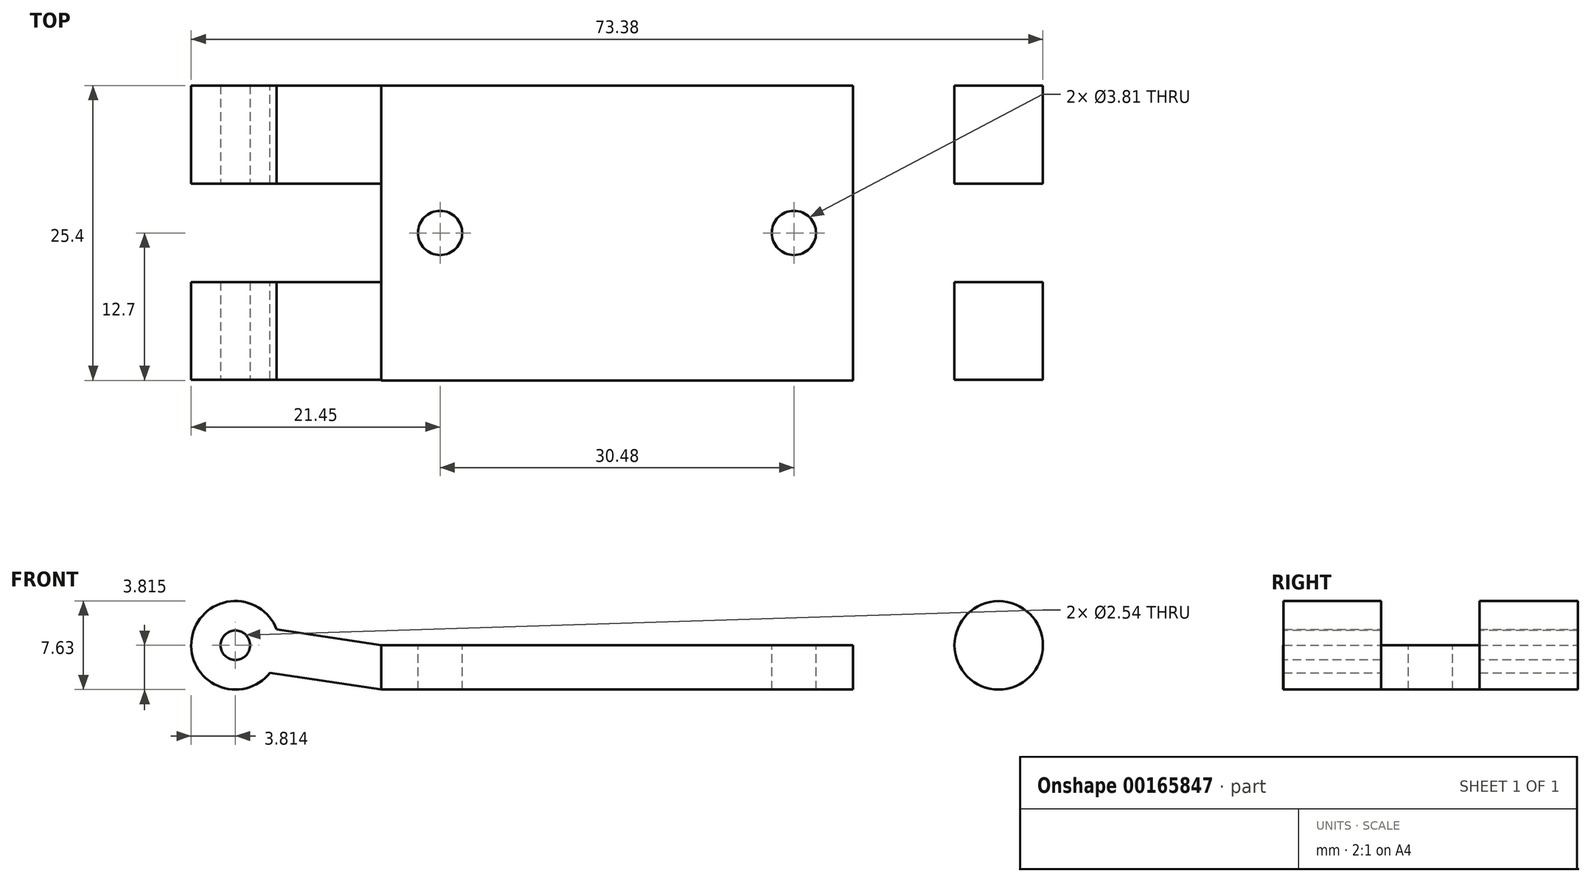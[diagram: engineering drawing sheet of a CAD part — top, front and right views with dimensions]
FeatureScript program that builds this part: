
annotation { "Feature Type Name" : "Feature", "Feature Type Description" : "" }
export const myFeature = defineFeature(function(context is Context, id is Id, definition is map)
    precondition{}
    {
        {
            var Q0;
            Q0=qCreatedBy(makeId("Front.planeOp"),FACE);
            var sketch = newSketch(context, id + "F0", { "sketchPlane" : qUnion([Q0])});
            skLineSegment(sketch, "E0.bottom", {"start": v(20.32, -1.9) * mm, "end": v(-20.32, -1.9) * mm});
            skLineSegment(sketch, "E0.top", {"start": v(20.32, 1.9) * mm, "end": v(-20.32, 1.9) * mm});
            skLineSegment(sketch, "E0.left", {"start": v(20.32, -1.9) * mm, "end": v(20.32, 1.9) * mm});
            skLineSegment(sketch, "E0.right", {"start": v(-20.32, -1.9) * mm, "end": v(-20.32, 1.9) * mm});
            skPoint(sketch, "E0.middle", {"position": v(0, 0) * mm});
            skLineSegment(sketch, "E1", {"start": v(20.32, 1.9) * mm, "end": v(32.88, 3.81) * mm});
            skLineSegment(sketch, "E2", {"start": v(20.32, -1.9) * mm, "end": v(32.88, 0) * mm});
            skLineSegment(sketch, "E3", {"start": v(-20.32, 1.9) * mm, "end": v(-32.88, 3.8) * mm});
            skLineSegment(sketch, "E4", {"start": v(-20.32, -1.9) * mm, "end": v(-32.88, 0) * mm});
            skLineSegment(sketch, "E5", {"start": v(32.88, 3.81) * mm, "end": v(32.88, 0) * mm});
            skLineSegment(sketch, "E6", {"start": v(-32.88, 3.8) * mm, "end": v(-32.88, 0) * mm});
            skPoint(sketch, "E7", {"position": v(32.88, 1.9) * mm});
            skPoint(sketch, "E8", {"position": v(-32.88, 1.9) * mm});
            skCircle(sketch, "E9", {"center": v(-32.88, 1.9) * mm, "radius": 3.81 * mm});
            skCircle(sketch, "E10", {"center": v(32.88, 1.9) * mm, "radius": 3.81 * mm});
            skLineSegment(sketch, "E11", {"start": v(-32.88, 0) * mm, "end": v(-20.32, -1.9) * mm});
            skLineSegment(sketch, "E12", {"start": v(32.88, 0) * mm, "end": v(20.32, -1.9) * mm});
            skLineSegment(sketch, "E13", {"start": v(20.32, 1.9) * mm, "end": v(20.32, -1.9) * mm});
            skSolve(sketch);
        }
        {
            var Q0;
            Q0=makeQuery(id+"F0.imprint","IMPRINT",FACE,{"disambiguationData":[TD([[makeQuery(id+"F0.imprint","IMPRINT",EDGE,{"derivedFrom":sQuery(id+"F0.wireOp",EDGE,"E0.bottom")}),-1.0]])]});
            extrude(context, id + "F1", {"entities" : qUnion([Q0]), "endBound" : BoundingType.SYMMETRIC, "depth" : 25.4 * mm});
        }
        {
            var Q0;
            {var subQ5=sQuery(id+"F0.wireOp",EDGE,"E13");Q0=makeQuery(id+"F0.imprint","IMPRINT",FACE,{"disambiguationData":[TD([[makeQuery(id+"F0.imprint","IMPRINT",EDGE,{"derivedFrom":subQ5}),1.0]])]});}
            var Q1;
            {var subQ5=sQuery(id+"F0.wireOp",EDGE,"E5");Q1=makeQuery(id+"F0.imprint","IMPRINT",FACE,{"disambiguationData":[TD([[makeQuery(id+"F0.imprint","IMPRINT",EDGE,{"derivedFrom":subQ5}),1.0]])]});}
            var Q2;
            {var subQ5=sQuery(id+"F0.wireOp",EDGE,"E5");Q2=makeQuery(id+"F0.imprint","IMPRINT",FACE,{"disambiguationData":[TD([[makeQuery(id+"F0.imprint","IMPRINT",EDGE,{"derivedFrom":subQ5}),-1.0]])]});}
            var Q3;
            {var subQ5=sQuery(id+"F0.wireOp",EDGE,"E0.right");Q3=makeQuery(id+"F0.imprint","IMPRINT",FACE,{"disambiguationData":[TD([[makeQuery(id+"F0.imprint","IMPRINT",EDGE,{"derivedFrom":subQ5}),1.0]])]});}
            var Q4;
            {var subQ5=sQuery(id+"F0.wireOp",EDGE,"E6");Q4=makeQuery(id+"F0.imprint","IMPRINT",FACE,{"disambiguationData":[TD([[makeQuery(id+"F0.imprint","IMPRINT",EDGE,{"derivedFrom":subQ5}),-1.0]])]});}
            var Q5;
            {var subQ5=sQuery(id+"F0.wireOp",EDGE,"E6");Q5=makeQuery(id+"F0.imprint","IMPRINT",FACE,{"disambiguationData":[TD([[makeQuery(id+"F0.imprint","IMPRINT",EDGE,{"derivedFrom":subQ5}),1.0]])]});}
            var Q6;
            Q6=makeQuery(id+"F1.opExtrude","SWEPT_FACE",FACE,{"disambiguationData":[OSD([sQuery(id+"F0.wireOp",EDGE,"E13")])]});
            extrude(context, id + "F2", {"entities" : qUnion([Q0, Q1, Q2, Q3, Q4, Q5]), "operationType" : NewBodyOperationType.ADD, "endBoundEntityFace" : qUnion([Q6]), "depth" : 12.65 * mm, "hasSecondDirection" : true, "secondDirectionOppositeDirection" : true, "secondDirectionDepth" : 12.7 * mm});
        }
        {
            var Q0;
            Q0=sQuery(id+"F0.wireOp",VERTEX,"E7");
            var Q1;
            Q1=sQuery(id+"F0.wireOp",VERTEX,"E8");
            var Q2;
            Q2=makeQuery(id+"F1.opExtrude","SWEPT_BODY",BODY,{"disambiguationData":[OSD([sQuery(id+"F0.wireOp",EDGE,"E0.bottom"),sQuery(id+"F0.wireOp",EDGE,"E0.top"),sQuery(id+"F0.wireOp",EDGE,"E0.right"),sQuery(id+"F0.wireOp",EDGE,"E13")])]});
            hole(context, id + "F3", {"style" : HoleStyle.SIMPLE, "endStyle" : HoleEndStyle.THROUGH, "holeDiameter" : 2.54 * mm, "startFromSketch" : true, "locations" : qUnion([Q0, Q1]), "scope" : qUnion([Q2]), "isTappedThrough" : true});
        }
        {
            var Q0;
            Q0=sQuery(id+"F0.wireOp",VERTEX,"E7");
            var Q1;
            Q1=sQuery(id+"F0.wireOp",VERTEX,"E8");
            var Q2;
            Q2=makeQuery(id+"F1.opExtrude","SWEPT_BODY",BODY,{"disambiguationData":[OSD([sQuery(id+"F0.wireOp",EDGE,"E0.bottom"),sQuery(id+"F0.wireOp",EDGE,"E0.top"),sQuery(id+"F0.wireOp",EDGE,"E0.right"),sQuery(id+"F0.wireOp",EDGE,"E13")])]});
            hole(context, id + "F4", {"style" : HoleStyle.SIMPLE, "endStyle" : HoleEndStyle.THROUGH, "oppositeDirection" : true, "holeDiameter" : 2.54 * mm, "startFromSketch" : true, "locations" : qUnion([Q0, Q1]), "scope" : qUnion([Q2]), "isTappedThrough" : true});
        }
        {
            var Q0;
            Q0=makeQuery(id+"F1.opExtrude","SWEPT_FACE",FACE,{"disambiguationData":[OSD([sQuery(id+"F0.wireOp",EDGE,"E0.top")])]});
            var sketch = newSketch(context, id + "F5", { "sketchPlane" : qUnion([Q0])});
            skPoint(sketch, "E14", {"position": v(15.24, 0) * mm});
            skPoint(sketch, "E15", {"position": v(-15.24, 0) * mm});
            skSolve(sketch);
        }
        {
            var Q0;
            {var subQ5=sQuery(id+"F0.wireOp",EDGE,"E13");Q0=makeQuery(id+"F0.imprint","IMPRINT",FACE,{"disambiguationData":[TD([[makeQuery(id+"F0.imprint","IMPRINT",EDGE,{"derivedFrom":subQ5}),1.0]])]});}
            var Q1;
            {var subQ5=sQuery(id+"F0.wireOp",EDGE,"E5");Q1=makeQuery(id+"F0.imprint","IMPRINT",FACE,{"disambiguationData":[TD([[makeQuery(id+"F0.imprint","IMPRINT",EDGE,{"derivedFrom":subQ5}),1.0]])]});}
            var Q2;
            {var subQ5=sQuery(id+"F0.wireOp",EDGE,"E5");Q2=makeQuery(id+"F0.imprint","IMPRINT",FACE,{"disambiguationData":[TD([[makeQuery(id+"F0.imprint","IMPRINT",EDGE,{"derivedFrom":subQ5}),-1.0]])]});}
            var Q3;
            Q3=sQuery(id+"F0.wireOp",EDGE,"E10");
            extrude(context, id + "F6", {"entities" : qUnion([Q0, Q1, Q2]), "operationType" : NewBodyOperationType.REMOVE, "surfaceEntities" : qUnion([Q3]), "endBound" : BoundingType.SYMMETRIC, "oppositeDirection" : true, "depth" : 8.46 * mm});
        }
        {
            var Q0;
            {var subQ5=sQuery(id+"F0.wireOp",EDGE,"E0.right");Q0=makeQuery(id+"F0.imprint","IMPRINT",FACE,{"disambiguationData":[TD([[makeQuery(id+"F0.imprint","IMPRINT",EDGE,{"derivedFrom":subQ5}),1.0]])]});}
            var Q1;
            {var subQ5=sQuery(id+"F0.wireOp",EDGE,"E6");Q1=makeQuery(id+"F0.imprint","IMPRINT",FACE,{"disambiguationData":[TD([[makeQuery(id+"F0.imprint","IMPRINT",EDGE,{"derivedFrom":subQ5}),1.0]])]});}
            var Q2;
            {var subQ5=sQuery(id+"F0.wireOp",EDGE,"E6");Q2=makeQuery(id+"F0.imprint","IMPRINT",FACE,{"disambiguationData":[TD([[makeQuery(id+"F0.imprint","IMPRINT",EDGE,{"derivedFrom":subQ5}),-1.0]])]});}
            extrude(context, id + "F7", {"entities" : qUnion([Q0, Q1, Q2]), "operationType" : NewBodyOperationType.REMOVE, "endBound" : BoundingType.SYMMETRIC, "depth" : 8.46 * mm});
        }
        {
            var Q0;
            Q0=sQuery(id+"F5.wireOp",VERTEX,"E15");
            var Q1;
            Q1=sQuery(id+"F5.wireOp",VERTEX,"E14");
            var Q2;
            Q2=makeQuery(id+"F1.opExtrude","SWEPT_BODY",BODY,{"disambiguationData":[OSD([sQuery(id+"F0.wireOp",EDGE,"E0.bottom"),sQuery(id+"F0.wireOp",EDGE,"E0.top"),sQuery(id+"F0.wireOp",EDGE,"E0.right"),sQuery(id+"F0.wireOp",EDGE,"E13")])]});
            hole(context, id + "F8", {"style" : HoleStyle.SIMPLE, "endStyle" : HoleEndStyle.THROUGH, "holeDiameter" : 3.8 * mm, "startFromSketch" : true, "locations" : qUnion([Q0, Q1]), "scope" : qUnion([Q2]), "isTappedThrough" : true});
        }
    });
